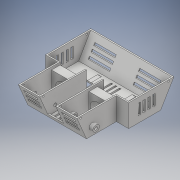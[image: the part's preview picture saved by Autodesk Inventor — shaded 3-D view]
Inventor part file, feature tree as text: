
AUTODESK INVENTOR PART (.ipt)
format: ipt  version: 2018.2 (Build 222227000, 227)  size: 544,768 bytes
history: native  units: mm
features: extrude x29, sketch x29, plane x2
ambient origin geometry x8: Origin, YZ Plane, XZ Plane, XY Plane, X Axis, Y Axis, Z Axis, Center Point
bodies: Solid1 (feature_tree)
feature tree (60):
  extrude  "Extrusion1"  Depth=56.0mm
  extrude  "Extrusion3"  Depth=23.0mm
  extrude  "Extrusion4"  Depth=30.0mm
  extrude  "Extrusion5"  Depth=3.0mm
  extrude  "Extrusion6"  Depth=39.0mm TaperAngle=0.0deg
  extrude  "Extrusion7"  Depth=2.4mm TaperAngle=0.0deg
  extrude  "Extrusion8"  Depth=2.4mm
  extrude  "Extrusion9"  Depth=2.4mm TaperAngle=0.0deg
  extrude  "Extrusion10"  Depth=70.0mm
  extrude  "Extrusion11"  Depth=2.4mm
  extrude  "Extrusion12"  Depth=2.4mm TaperAngle=0.0deg
  extrude  "Extrusion13"  Depth=2.4mm
  extrude  "Extrusion14"  Depth=2.4mm
  extrude  "Extrusion16"  Depth=30.0mm TaperAngle=0.0deg
  extrude  "Extrusion17"  Depth=15.0mm
  extrude  "Extrusion18"  Depth=12.0mm
  extrude  "Extrusion26"  Depth=7.0mm
  extrude  "Extrusion30"  Depth=43.0mm
  extrude  "Extrusion33"  Depth=15.0mm
  extrude  "Extrusion34"  Depth=12.0mm
  extrude  "Extrusion35"  Depth=3.0mm
  extrude  "Extrusion36"  Depth=3.0mm
  extrude  "Extrusion37"  Depth=110.0mm
  plane  "Work Plane1"
  extrude  "Extrusion38"  Depth=5.0mm
  plane  "Work Plane2"
  extrude  "Extrusion39"  Depth=4.0mm TaperAngle=0.0deg
  extrude  "Extrusion40"  Depth=34.0mm TaperAngle=0.0deg
  extrude  "Extrusion41"  Depth=25.0mm
  extrude  "Extrusion42"  Depth=11.0mm TaperAngle=0.0deg
  extrude  "Extrusion43"  Depth=70.0mm TaperAngle=0.0deg
  sketch  "Sketch1"  dims[d0=110.0mm d1=56.0mm]
  sketch  "Sketch3"  dims[d2=23.0mm d3=23.0mm]
  sketch  "Sketch4"  dims[d7=30.0mm d8=30.0mm]
  sketch  "Sketch5"  dims[d9=3.0mm d10=0.0mm d17=60.0mm]
  sketch  "Sketch6"  dims[d18=2.4mm d19=39.0mm d20=0.0mm]
  sketch  "Sketch7"  dims[d21=25.0mm d22=2.4mm d23=0.0mm]
  sketch  "Sketch8"  dims[d24=2.4mm d25=0.0mm d26=2.4mm]
  sketch  "Sketch10"  dims[d27=153.6mm d28=0.0mm d30=2.4mm d31=0.0mm]
  sketch  "Sketch11"  dims[d32=2.4mm d33=0.0mm d37=70.0mm]
  sketch  "Sketch12"  dims[d38=2.4mm d39=2.4mm]
  sketch  "Sketch13"  dims[d40=39.0mm d41=0.0mm d42=2.4mm d43=0.0mm]
  sketch  "Sketch14"  dims[d44=2.4mm d45=0.0mm d46=2.4mm]
  sketch  "Sketch15"  dims[d47=36.0mm d48=0.0mm d49=2.4mm]
  sketch  "Sketch17"  dims[d50=36.0mm d51=0.0mm d52=30.0mm d53=0.0mm]
  sketch  "Sketch18"  dims[d61=43.0mm d62=15.0mm]
  sketch  "Sketch19"  dims[d63=45.0mm d64=12.0mm]
  sketch  "Sketch27"  dims[d65=7.0mm d66=0.0mm d67=5.25mm]
  sketch  "Sketch31"  dims[d68=650.0mm d69=0.0mm d70=43.0mm]
  sketch  "Sketch32"  dims[d71=45.0mm d72=15.0mm]
  sketch  "Sketch33"  dims[d73=12.0mm d74=5.25mm]
  sketch  "Sketch34"  dims[d75=7.0mm d76=0.0mm d170=3.0mm]
  sketch  "Sketch35"  dims[d171=110.0mm d172=3.0mm]
  sketch  "Sketch36"  dims[d173=3.0mm d174=110.0mm]
  sketch  "Sketch37"  dims[d175=13.5mm d176=5.0mm]
  sketch  "Sketch38"  dims[d177=5.0mm d178=4.0mm d179=0.0mm]
  sketch  "Sketch39"  dims[d206=5.0mm d207=34.0mm d208=0.0mm]
  sketch  "Sketch40"  dims[d209=42.0mm d228=25.0mm]
  sketch  "Sketch41"  dims[d229=25.0mm d230=11.0mm d231=0.0mm]
  sketch  "Sketch42"  dims[d232=5.0mm d233=0.0mm d234=70.0mm d235=0.0mm d236=7.0mm d237=35.0mm d238=7.0mm d239=7.0mm d240=35.0mm d241=14.0mm d242=23.0mm d243=0.0mm d244=20.0mm d245=4.0mm d246=4.0mm d247=4.0mm d248=4.0mm d249=156.0mm d250=0.0mm d251=3.0mm d252=3.0mm d253=7.0mm d254=50.0mm d255=0.0mm d256=-25.0mm d257=25.0mm d258=4.0mm d259=4.0mm d260=4.0mm d261=8.0mm d262=25.0mm d263=4.0mm d264=4.0mm d265=8.0mm d266=40.0mm d267=0.0mm d268=25.0mm d269=150.0mm d270=40.0mm d271=4.0mm d272=4.0mm d273=4.0mm d274=40.0mm d275=4.0mm d276=22.0mm d277=22.0mm d278=40.0mm d279=0.0mm d280=10.0mm d281=5.0mm d282=0.0mm d283=10.0mm d284=5.0mm d285=0.0mm d286=23.0mm d287=30.0mm d288=23.0mm d289=7.0mm d290=7.0mm d291=5.0mm d292=0.0mm d293=40.0mm d294=3.0mm d295=3.0mm d296=7.0mm d297=156.0mm d298=0.0mm d299=100.0mm d300=0.0mm]
